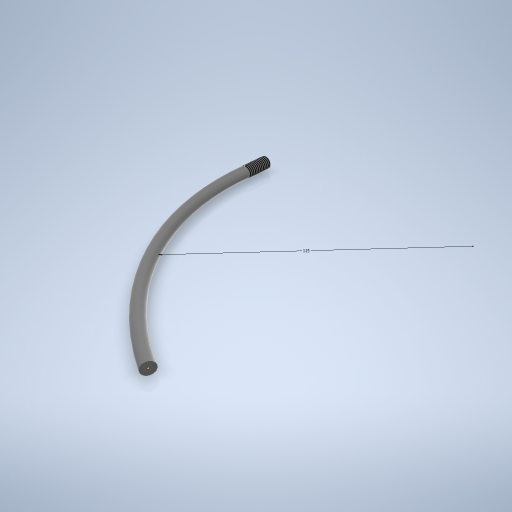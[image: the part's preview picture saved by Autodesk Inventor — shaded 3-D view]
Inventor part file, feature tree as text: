
AUTODESK INVENTOR PART (.ipt)
format: ipt  version: 2024.2 (Build 282272000, 272)  size: 288,256 bytes
history: native  units: mm
features: sketch x2, sweep x1, thread x1, other x1, fillet x1
ambient origin geometry x8: Origin, YZ Plane, XZ Plane, XY Plane, X Axis, Y Axis, Z Axis, Center Point
bodies: Volumenkörper1 (feature_tree)
feature tree (6):
  sweep  "Sweeping1"
  thread  "Gewinde1"  [1 undecoded]
  other  "3D-Skizze2"
  fillet  "Rundung1"  Radius=67.0mm
  sketch  "Skizze2"  dims[d1=6.0mm d2=115.0mm d3=120.0mm d4=67.0mm]
  sketch  "Skizze3"  dims[d5=0.0mm d6=0.0mm d7=2.0mm d8=13.0mm d9=18.0mm d10=0.0mm d14=115.0mm]
note: 1 required parameter value undecoded (feature->parameter linkage not recoverable at this tier; creation-order binding heuristic only, values carry confidence <= 0.55)
